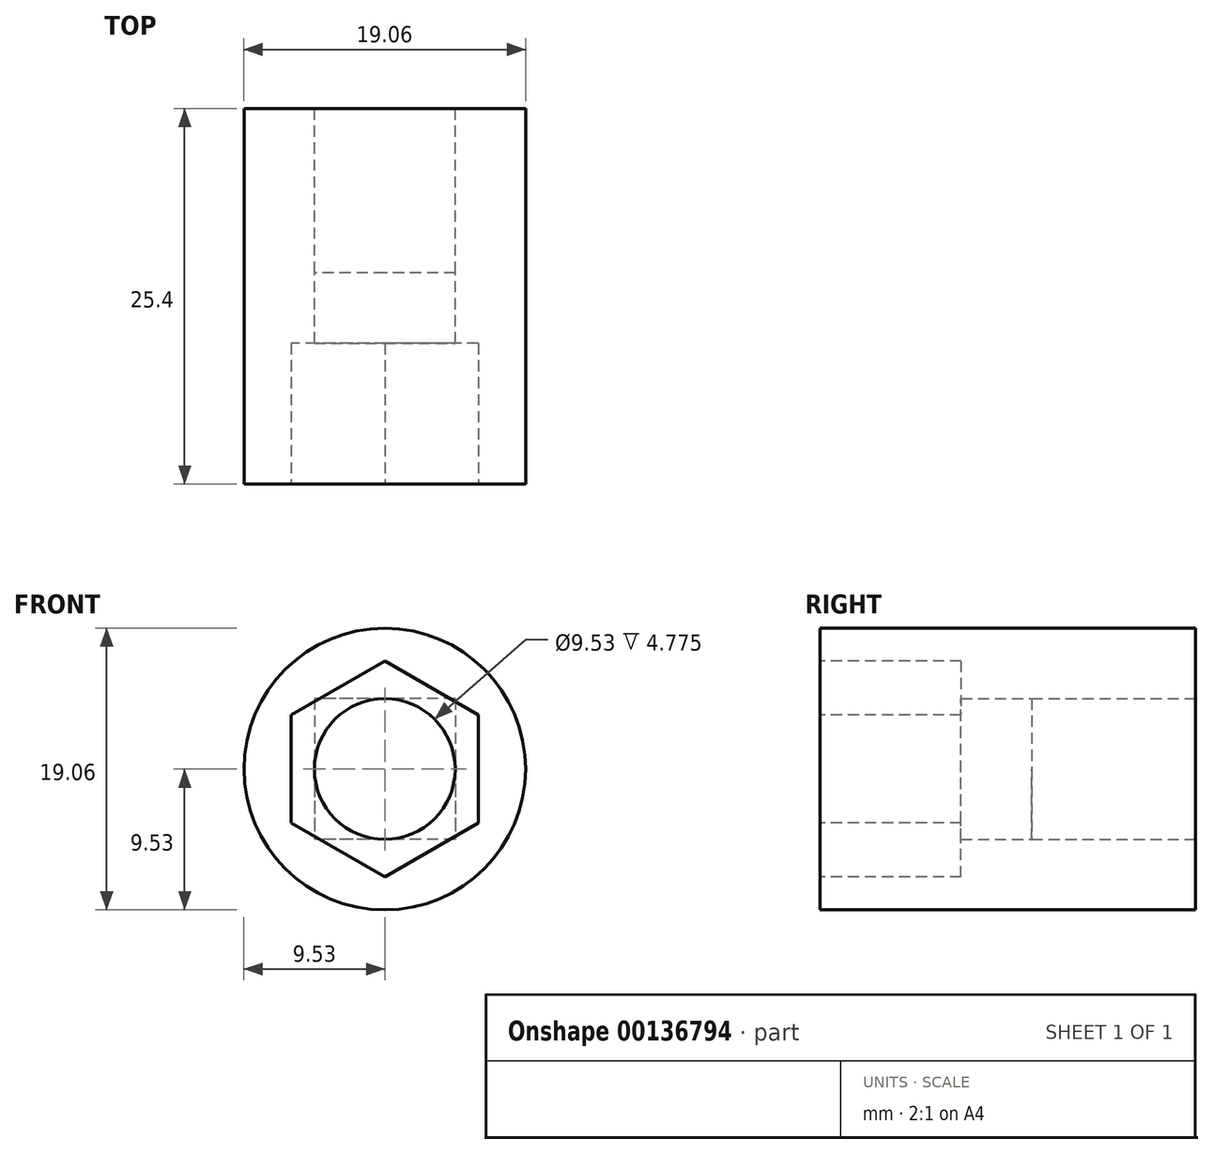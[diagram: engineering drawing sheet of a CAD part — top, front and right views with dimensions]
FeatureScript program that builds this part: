
annotation { "Feature Type Name" : "Feature", "Feature Type Description" : "" }
export const myFeature = defineFeature(function(context is Context, id is Id, definition is map)
    precondition{}
    {
        {
            var Q0;
            Q0=qCreatedBy(makeId("Front.planeOp"),FACE);
            var sketch = newSketch(context, id + "F0", { "sketchPlane" : qUnion([Q0])});
            skCircle(sketch, "E0", {"center": v(0, 0) * mm, "radius": 9.53 * mm});
            skSolve(sketch);
        }
        {
            var Q0;
            Q0 = qSketchRegion(id + "F0", true);
            extrude(context, id + "F1", {"entities" : qUnion([Q0]), "depth" : 25.4 * mm});
        }
        {
            var Q0;
            Q0=makeQuery(id+"F1.opExtrude","CAP_FACE",FACE,{"disambiguationData":[OSD([sQuery(id+"F0.wireOp",EDGE,"E0")])],"isStart":true});
            var sketch = newSketch(context, id + "F2", { "sketchPlane" : qUnion([Q0])});
            skLineSegment(sketch, "E1.bottom", {"start": v(-4.76, 4.76) * mm, "end": v(4.76, 4.76) * mm});
            skLineSegment(sketch, "E1.top", {"start": v(-4.76, -4.76) * mm, "end": v(4.76, -4.76) * mm});
            skLineSegment(sketch, "E1.left", {"start": v(-4.76, 4.76) * mm, "end": v(-4.76, -4.76) * mm});
            skLineSegment(sketch, "E1.right", {"start": v(4.76, 4.76) * mm, "end": v(4.76, -4.76) * mm});
            skPoint(sketch, "E1.middle", {"position": v(0, 0) * mm});
            skCircle(sketch, "E2", {"center": v(0, 0) * mm, "radius": 4.76 * mm});
            skSolve(sketch);
        }
        {
            var Q0;
            {var subQ0=sQuery(id+"F2.wireOp",EDGE,"E2");var subQ1=makeQuery(id+"F2.imprint","INTERSECT",VERTEX,{"derivedFrom":[sQuery(id+"F2.wireOp",EDGE,"E1.bottom"),subQ0]});Q0=makeQuery(id+"F2.imprint","IMPRINT",FACE,{"disambiguationData":[TD([[makeQuery(id+"F2.imprint","IMPRINT",EDGE,{"disambiguationData":[TD([[subQ1,1.0]])],"derivedFrom":subQ0}),1.0]])]});}
            extrude(context, id + "F3", {"entities" : qUnion([Q0]), "operationType" : NewBodyOperationType.REMOVE, "endBound" : BoundingType.THROUGH_ALL, "oppositeDirection" : true, "depth" : 25.4 * mm});
        }
        {
            var Q0;
            Q0 = qSketchRegion(id + "F2", true);
            extrude(context, id + "F4", {"entities" : qUnion([Q0]), "operationType" : NewBodyOperationType.REMOVE, "oppositeDirection" : true, "depth" : 11.1 * mm});
        }
        {
            var Q0;
            Q0=makeQuery(id+"F1.opExtrude","CAP_FACE",FACE,{"disambiguationData":[OSD([sQuery(id+"F0.wireOp",EDGE,"E0")])],"isStart":false});
            var sketch = newSketch(context, id + "F5", { "sketchPlane" : qUnion([Q0])});
            skCircle(sketch, "E3.cCircle", {"center": v(0, 0) * mm, "radius": 6.32 * mm, "construction": true});
            skLineSegment(sketch, "E3.0", {"start": v(-6.32, -3.65) * mm, "end": v(-6.32, 3.65) * mm});
            skLineSegment(sketch, "E3.1", {"start": v(-6.32, 3.65) * mm, "end": v(0, 7.3) * mm});
            skLineSegment(sketch, "E3.2", {"start": v(0, 7.3) * mm, "end": v(6.32, 3.65) * mm});
            skLineSegment(sketch, "E3.3", {"start": v(6.32, 3.65) * mm, "end": v(6.32, -3.65) * mm});
            skLineSegment(sketch, "E3.4", {"start": v(6.32, -3.65) * mm, "end": v(0, -7.3) * mm});
            skLineSegment(sketch, "E3.5", {"start": v(0, -7.3) * mm, "end": v(-6.32, -3.65) * mm});
            skPoint(sketch, "E3.0.midPoint", {"position": v(-6.32, 0) * mm});
            skSolve(sketch);
        }
        {
            var Q0;
            Q0 = qSketchRegion(id + "F5", true);
            extrude(context, id + "F6", {"entities" : qUnion([Q0]), "operationType" : NewBodyOperationType.REMOVE, "oppositeDirection" : true, "depth" : 9.52 * mm});
        }
    });
